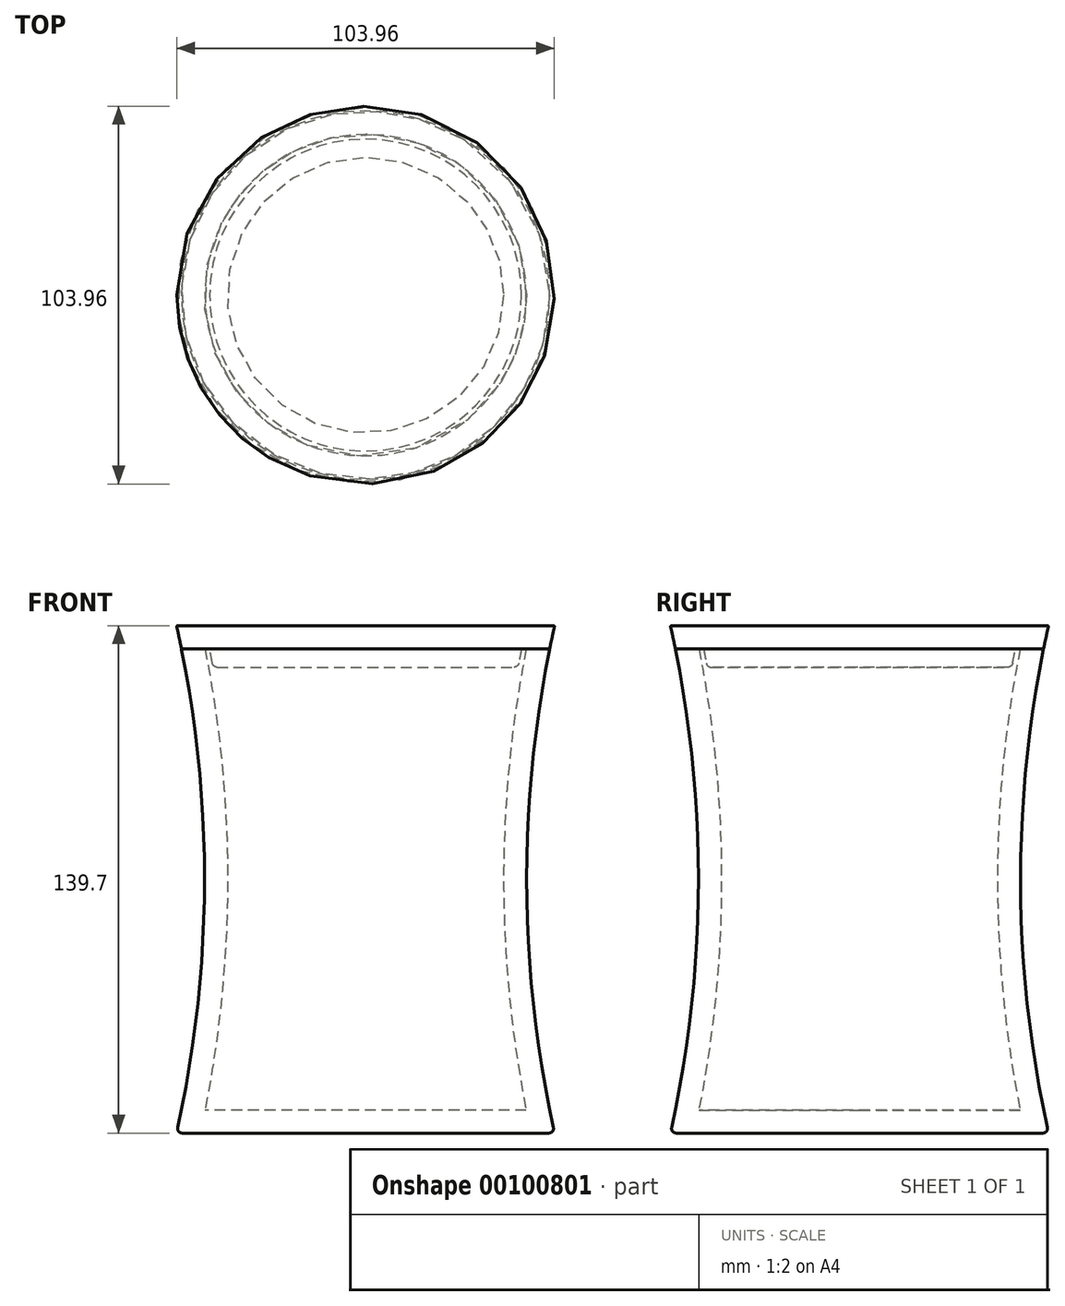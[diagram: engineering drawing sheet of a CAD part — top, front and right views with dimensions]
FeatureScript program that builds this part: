
annotation { "Feature Type Name" : "Feature", "Feature Type Description" : "" }
export const myFeature = defineFeature(function(context is Context, id is Id, definition is map)
    precondition{}
    {
        {
            var Q0;
            Q0=qCreatedBy(makeId("Front.planeOp"),FACE);
            var sketch = newSketch(context, id + "F0", { "sketchPlane" : qUnion([Q0])});
            skCircle(sketch, "E0", {"center": v(-612.85, 0) * mm, "radius": 320.68 * mm});
            skLineSegment(sketch, "E1", {"start": v(-298.53, 63.5) * mm, "end": v(-298.53, -63.5) * mm, "construction": true});
            skCircle(sketch, "E2.0", {"center": v(-612.85, 0) * mm, "radius": 327.03 * mm});
            skLineSegment(sketch, "E3", {"start": v(-298.53, -63.5) * mm, "end": v(-247.83, -63.5) * mm});
            skLineSegment(sketch, "E4", {"start": v(-299.88, -69.85) * mm, "end": v(-247.83, -69.85) * mm});
            skLineSegment(sketch, "E5", {"start": v(-247.83, -69.85) * mm, "end": v(-247.83, -63.5) * mm});
            skLineSegment(sketch, "E6", {"start": v(-299.88, 69.85) * mm, "end": v(-247.83, 69.85) * mm});
            skLineSegment(sketch, "E7", {"start": v(-247.83, 69.85) * mm, "end": v(-247.83, 63.5) * mm});
            skLineSegment(sketch, "E8", {"start": v(-247.83, 63.5) * mm, "end": v(-298.53, 63.5) * mm});
            skLineSegment(sketch, "E9", {"start": v(-247.83, 90.36) * mm, "end": v(-247.83, -90.28) * mm, "construction": true});
            skCircle(sketch, "E10.0", {"center": v(-612.85, 0) * mm, "radius": 328.3 * mm});
            skLineSegment(sketch, "E11", {"start": v(-289.8, 58.42) * mm, "end": v(-247.83, 58.42) * mm});
            skLineSegment(sketch, "E12", {"start": v(-247.83, 58.42) * mm, "end": v(-247.83, 63.5) * mm});
            skSolve(sketch);
        }
        {
            var Q0;
            {var subQ0=sQuery(id+"F0.wireOp",EDGE,"E3");var subQ1=sQuery(id+"F0.wireOp",EDGE,"E0");var subQ2=makeQuery(id+"F0.imprint","INTERSECT",VERTEX,{"derivedFrom":[subQ1,subQ0]});Q0=makeQuery(id+"F0.imprint","IMPRINT",FACE,{"disambiguationData":[TD([[makeQuery(id+"F0.imprint","IMPRINT",EDGE,{"disambiguationData":[TD([[subQ2,-1.0]])],"derivedFrom":subQ1}),-1.0]])]});}
            var Q1;
            {var subQ0=sQuery(id+"F0.wireOp",EDGE,"E3");var subQ1=sQuery(id+"F0.wireOp",EDGE,"E0");var subQ2=makeQuery(id+"F0.imprint","INTERSECT",VERTEX,{"derivedFrom":[subQ1,subQ0]});Q1=makeQuery(id+"F0.imprint","IMPRINT",FACE,{"disambiguationData":[TD([[makeQuery(id+"F0.imprint","IMPRINT",EDGE,{"disambiguationData":[TD([[subQ2,1.0]])],"derivedFrom":subQ1}),-1.0]])]});}
            var Q2;
            {var subQ0=sQuery(id+"F0.wireOp",EDGE,"E4");var subQ1=sQuery(id+"F0.wireOp",EDGE,"E2.0");var subQ2=makeQuery(id+"F0.imprint","INTERSECT",VERTEX,{"derivedFrom":[subQ1,subQ0]});Q2=makeQuery(id+"F0.imprint","IMPRINT",FACE,{"disambiguationData":[TD([[makeQuery(id+"F0.imprint","IMPRINT",EDGE,{"disambiguationData":[TD([[subQ2,-1.0]])],"derivedFrom":subQ1}),-1.0]])]});}
            var Q3;
            {var subQ0=sQuery(id+"F0.wireOp",EDGE,"E5");Q3=makeQuery(id+"F0.imprint","IMPRINT",FACE,{"disambiguationData":[TD([[makeQuery(id+"F0.imprint","IMPRINT",EDGE,{"derivedFrom":subQ0}),1.0]])]});}
            var Q4;
            Q4=sQuery(id+"F0.wireOp",EDGE,"E9");
            revolve(context, id + "F1", {"entities" : qUnion([Q0, Q1, Q2, Q3]), "axis" : qUnion([Q4]), "revolveType" : RevolveType.FULL});
        }
        {
            var Q0;
            {var subQ0=sQuery(id+"F0.wireOp",EDGE,"E6");var subQ1=sQuery(id+"F0.wireOp",EDGE,"E0");var subQ2=makeQuery(id+"F0.imprint","INTERSECT",VERTEX,{"derivedFrom":[subQ1,subQ0]});Q0=makeQuery(id+"F0.imprint","IMPRINT",FACE,{"disambiguationData":[TD([[makeQuery(id+"F0.imprint","IMPRINT",EDGE,{"disambiguationData":[TD([[subQ2,1.0]])],"derivedFrom":subQ1}),-1.0]])]});}
            var Q1;
            {var subQ0=sQuery(id+"F0.wireOp",EDGE,"E6");var subQ1=sQuery(id+"F0.wireOp",EDGE,"E2.0");var subQ2=makeQuery(id+"F0.imprint","INTERSECT",VERTEX,{"derivedFrom":[subQ1,subQ0]});Q1=makeQuery(id+"F0.imprint","IMPRINT",FACE,{"disambiguationData":[TD([[makeQuery(id+"F0.imprint","IMPRINT",EDGE,{"disambiguationData":[TD([[subQ2,1.0]])],"derivedFrom":subQ1}),-1.0]])]});}
            var Q2;
            {var subQ0=sQuery(id+"F0.wireOp",EDGE,"E7");Q2=makeQuery(id+"F0.imprint","IMPRINT",FACE,{"disambiguationData":[TD([[makeQuery(id+"F0.imprint","IMPRINT",EDGE,{"derivedFrom":subQ0}),-1.0]])]});}
            var Q3;
            {var subQ4=sQuery(id+"F0.wireOp",EDGE,"E11");Q3=makeQuery(id+"F0.imprint","IMPRINT",FACE,{"disambiguationData":[TD([[makeQuery(id+"F0.imprint","IMPRINT",EDGE,{"derivedFrom":subQ4}),1.0]])]});}
            var Q4;
            Q4=sQuery(id+"F0.wireOp",EDGE,"E9");
            revolve(context, id + "F2", {"entities" : qUnion([Q0, Q1, Q2, Q3]), "axis" : qUnion([Q4]), "revolveType" : RevolveType.FULL});
        }
        {
            var Q0;
            Q0=makeQuery(id+"F1.opRevolve","SWEPT_EDGE",EDGE,{"disambiguationData":[OSD([sQuery(id+"F0.wireOp",EDGE,"E0"),sQuery(id+"F0.wireOp",EDGE,"E4")])]});
            var Q1;
            Q1=makeQuery(id+"F2.opRevolve","SWEPT_EDGE",EDGE,{"disambiguationData":[OSD([sQuery(id+"F0.wireOp",EDGE,"E10.0"),sQuery(id+"F0.wireOp",EDGE,"E11")])]});
            fillet(context, id + "F3", {"entities" : qUnion([Q0, Q1]), "radius" : 1.27 * mm, "tangentPropagation" : true, "allowEdgeOverflow" : false});
        }
        {
            var Q0;
            Q0=makeQuery(id+"F2.opRevolve","SWEPT_EDGE",EDGE,{"disambiguationData":[OSD([sQuery(id+"F0.wireOp",EDGE,"E0"),sQuery(id+"F0.wireOp",EDGE,"E6")])]});
            var Q1;
            Q1=makeQuery(id+"F1.opRevolve","SWEPT_EDGE",EDGE,{"disambiguationData":[OSD([sQuery(id+"F0.wireOp",EDGE,"E0"),sQuery(id+"F0.wireOp",EDGE,"E8")])]});
            fillet(context, id + "F4", {"entities" : qUnion([Q0, Q1]), "radius" : 0.25 * mm, "tangentPropagation" : true, "allowEdgeOverflow" : false});
        }
    });
